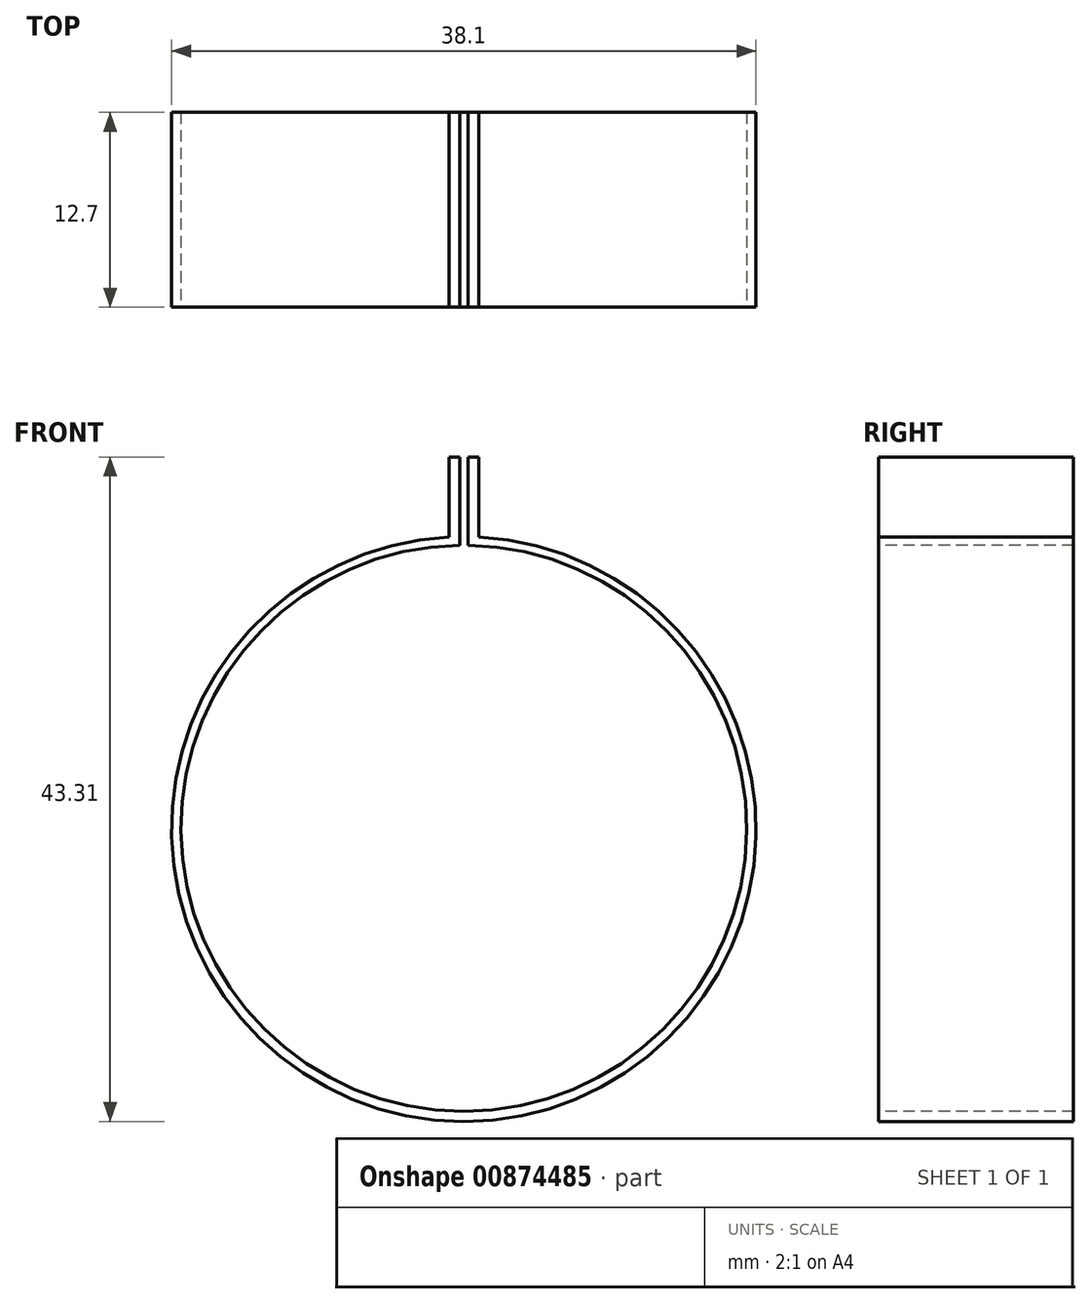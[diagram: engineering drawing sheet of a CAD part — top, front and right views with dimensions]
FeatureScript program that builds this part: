
annotation { "Feature Type Name" : "Feature", "Feature Type Description" : "" }
export const myFeature = defineFeature(function(context is Context, id is Id, definition is map)
    precondition{}
    {
        {
            var Q0;
            Q0=qCreatedBy(makeId("Front.planeOp"),FACE);
            var sketch = newSketch(context, id + "F0", { "sketchPlane" : qUnion([Q0])});
            skLineSegment(sketch, "E0", {"start": v(-0.27, 43.3) * mm, "end": v(-0.97, 43.3) * mm});
            skLineSegment(sketch, "E1", {"start": v(-0.97, 43.3) * mm, "end": v(-0.97, 38.08) * mm});
            skLineSegment(sketch, "E2.MirrorCS", {"start": v(0.97, 43.3) * mm, "end": v(0.97, 38.08) * mm});
            skLineSegment(sketch, "E3.MirrorCS", {"start": v(0.27, 43.3) * mm, "end": v(0.97, 43.3) * mm});
            skArc(sketch, "E4", {"start": v(-0.97, 38.08) * mm, "mid": v(0, 0) * mm, "end": v(0.97, 38.08) * mm});
            skLineSegment(sketch, "E5", {"start": v(-0.27, 43.3) * mm, "end": v(-0.27, 37.55) * mm});
            skLineSegment(sketch, "E6.MirrorCS", {"start": v(0.27, 43.3) * mm, "end": v(0.27, 37.55) * mm});
            skPoint(sketch, "E7.orphan", {"position": v(0, 43.3) * mm});
            skArc(sketch, "E8", {"start": v(-0.27, 37.55) * mm, "mid": v(0, 0.66) * mm, "end": v(0.27, 37.55) * mm});
            skSolve(sketch);
        }
        {
            var Q0;
            Q0 = qSketchRegion(id + "F0", true);
            extrude(context, id + "F1", {"entities" : qUnion([Q0]), "oppositeDirection" : true, "depth" : 12.7 * mm, "offsetDistance" : 25.4 * mm});
        }
    });
